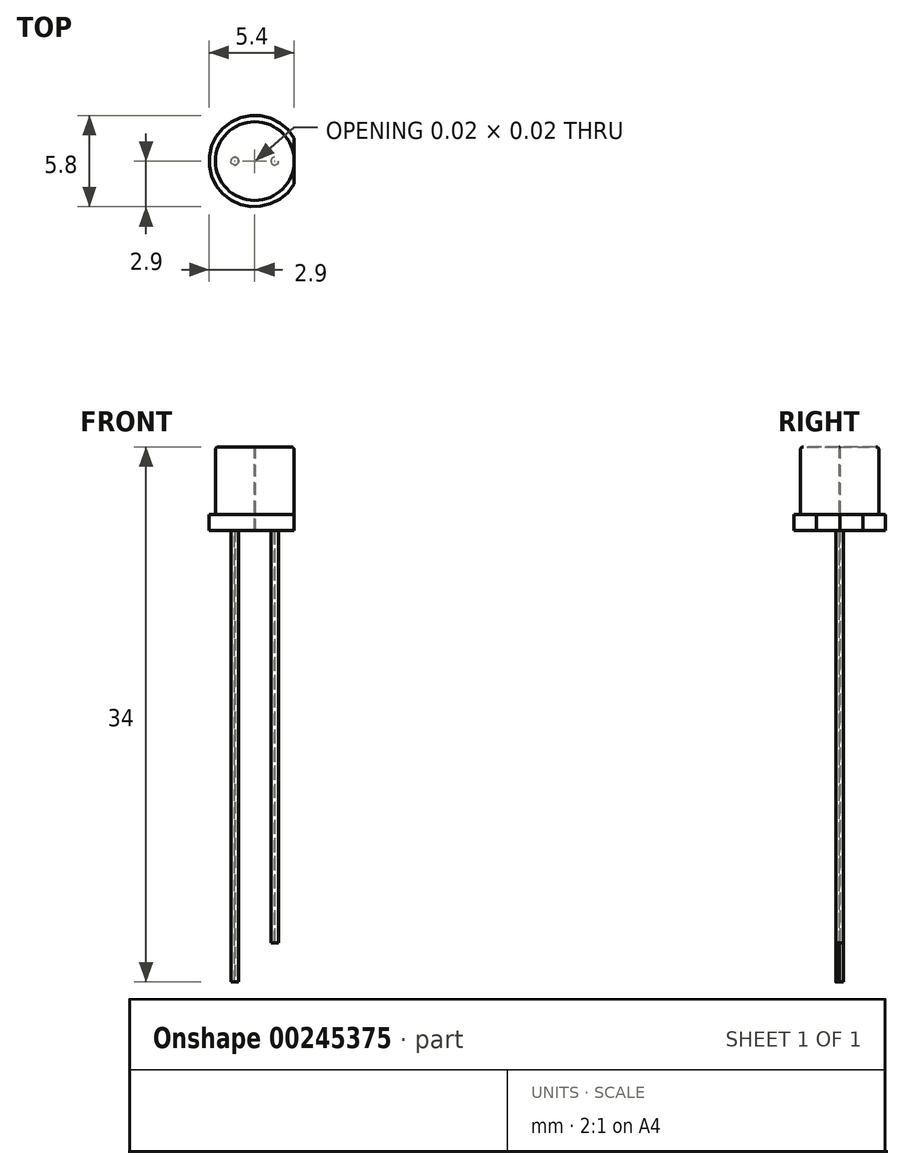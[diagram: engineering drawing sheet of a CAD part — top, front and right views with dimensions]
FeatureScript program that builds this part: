
annotation { "Feature Type Name" : "Feature", "Feature Type Description" : "" }
export const myFeature = defineFeature(function(context is Context, id is Id, definition is map)
    precondition{}
    {
        {
            var Q0;
            Q0=qCreatedBy(makeId("Front.planeOp"),FACE);
            var sketch = newSketch(context, id + "F0", { "sketchPlane" : qUnion([Q0])});
            skLineSegment(sketch, "E0", {"start": v(0, 0) * mm, "end": v(0, 4.3) * mm});
            skLineSegment(sketch, "E1", {"start": v(0, 4.3) * mm, "end": v(2.5, 4.3) * mm});
            skLineSegment(sketch, "E2", {"start": v(2.5, 4.3) * mm, "end": v(2.5, 0) * mm});
            skLineSegment(sketch, "E3", {"start": v(2.5, 0) * mm, "end": v(0, 0) * mm});
            skLineSegment(sketch, "E4", {"start": v(0, 0) * mm, "end": v(0, -1) * mm});
            skLineSegment(sketch, "E5", {"start": v(0, -1) * mm, "end": v(2.9, -1) * mm});
            skLineSegment(sketch, "E6", {"start": v(2.9, -1) * mm, "end": v(2.9, 0) * mm});
            skLineSegment(sketch, "E7", {"start": v(2.9, 0) * mm, "end": v(2.5, 0) * mm});
            skLineSegment(sketch, "E8", {"start": v(1.27, -1) * mm, "end": v(1.27, -27.2) * mm});
            skLineSegment(sketch, "E9", {"start": v(1.27, -27.2) * mm, "end": v(1.52, -27.2) * mm});
            skLineSegment(sketch, "E10", {"start": v(1.52, -27.2) * mm, "end": v(1.52, -1) * mm, "construction": true});
            skLineSegment(sketch, "E11", {"start": v(1.27, -27.2) * mm, "end": v(1.02, -27.2) * mm});
            skLineSegment(sketch, "E12", {"start": v(1.02, -27.2) * mm, "end": v(1.02, -1) * mm});
            skLineSegment(sketch, "E13.MirrorCS", {"start": v(-1.02, -27.2) * mm, "end": v(-1.02, -1) * mm});
            skLineSegment(sketch, "E14", {"start": v(-1.27, -1) * mm, "end": v(-1.02, -1) * mm});
            skLineSegment(sketch, "E15", {"start": v(-1.27, -29.7) * mm, "end": v(-1.02, -29.7) * mm});
            skLineSegment(sketch, "E16", {"start": v(-1.02, -29.7) * mm, "end": v(-1.02, -27.2) * mm});
            skLineSegment(sketch, "E17", {"start": v(-1.27, -29.7) * mm, "end": v(-1.27, -1) * mm});
            skSolve(sketch);
        }
        {
            var Q0;
            Q0=makeQuery(id+"F0.imprint","IMPRINT",FACE,{"disambiguationData":[TD([[makeQuery(id+"F0.imprint","IMPRINT",EDGE,{"derivedFrom":sQuery(id+"F0.wireOp",EDGE,"E0")}),-1.0]])]});
            var Q1;
            Q1=makeQuery(id+"F0.imprint","IMPRINT",FACE,{"disambiguationData":[TD([[makeQuery(id+"F0.imprint","IMPRINT",EDGE,{"derivedFrom":sQuery(id+"F0.wireOp",EDGE,"E3")}),1.0]])]});
            extrude(context, id + "F1", {"entities" : qUnion([Q0, Q1]), "depth" : 0.01 * mm});
        }
        {
            var Q0;
            Q0=makeQuery(id+"F1.opExtrude","CAP_FACE",FACE,{"disambiguationData":[OSD([sQuery(id+"F0.wireOp",EDGE,"E0"),sQuery(id+"F0.wireOp",EDGE,"E1"),sQuery(id+"F0.wireOp",EDGE,"E2"),sQuery(id+"F0.wireOp",EDGE,"E4"),sQuery(id+"F0.wireOp",EDGE,"E5"),sQuery(id+"F0.wireOp",EDGE,"E6"),sQuery(id+"F0.wireOp",EDGE,"E7")])],"isStart":false});
            var Q1;
            Q1=makeQuery(id+"F1.opExtrude","CAP_EDGE",EDGE,{"disambiguationData":[OSD([sQuery(id+"F0.wireOp",EDGE,"E0"),sQuery(id+"F0.wireOp",EDGE,"E4")])],"isStart":true});
            revolve(context, id + "F2", {"operationType" : NewBodyOperationType.ADD, "entities" : qUnion([Q0]), "axis" : qUnion([Q1]), "revolveType" : RevolveType.FULL});
        }
        {
            var Q0;
            Q0=qCreatedBy(makeId("Right.planeOp"),FACE);
            cPlane(context, id + "F3", {"entities" : qUnion([Q0]), "cplaneType" : CPlaneType.OFFSET, "offset" : 2.5 * mm, "width" : 150 * mm, "height" : 150 * mm});
        }
        {
            var Q0;
            Q0=qCreatedBy(id+"F3.planeOp",FACE);
            var sketch = newSketch(context, id + "F4", { "sketchPlane" : qUnion([Q0])});
            skLineSegment(sketch, "E18.bottom", {"start": v(1.5, -1.2) * mm, "end": v(-1.5, -1.2) * mm});
            skLineSegment(sketch, "E18.top", {"start": v(1.5, 1.2) * mm, "end": v(-1.5, 1.2) * mm});
            skLineSegment(sketch, "E18.left", {"start": v(1.5, -1.2) * mm, "end": v(1.5, 1.2) * mm});
            skLineSegment(sketch, "E18.right", {"start": v(-1.5, -1.2) * mm, "end": v(-1.5, 1.2) * mm});
            skPoint(sketch, "E18.middle", {"position": v(0, 0) * mm});
            skSolve(sketch);
        }
        {
            var Q0;
            Q0 = qSketchRegion(id + "F4", true);
            extrude(context, id + "F5", {"entities" : qUnion([Q0]), "operationType" : NewBodyOperationType.REMOVE, "depth" : 2 * mm});
        }
        {
            var Q0;
            {var subQ0=sQuery(id+"F0.wireOp",EDGE,"E8");Q0=makeQuery(id+"F0.imprint","IMPRINT",FACE,{"disambiguationData":[TD([[makeQuery(id+"F0.imprint","IMPRINT",EDGE,{"derivedFrom":subQ0}),-1.0]])]});}
            extrude(context, id + "F6", {"entities" : qUnion([Q0]), "operationType" : NewBodyOperationType.ADD, "depth" : 0.01 * mm});
        }
        {
            var Q0;
            Q0=makeQuery(id+"F0.imprint","IMPRINT",FACE,{"disambiguationData":[TD([[makeQuery(id+"F0.imprint","IMPRINT",EDGE,{"derivedFrom":sQuery(id+"F0.wireOp",EDGE,"E13.MirrorCS")}),1.0]])]});
            extrude(context, id + "F7", {"entities" : qUnion([Q0]), "operationType" : NewBodyOperationType.ADD, "depth" : 0.01 * mm});
        }
        {
            var Q0;
            Q0=makeQuery(id+"F7.opExtrude","CAP_FACE",FACE,{"disambiguationData":[OSD([sQuery(id+"F0.wireOp",EDGE,"E13.MirrorCS"),sQuery(id+"F0.wireOp",EDGE,"ac1886b3-cde3-48e8-9153-fe326fcb880c0.MirrorCS"),sQuery(id+"F0.wireOp",EDGE,"E14"),sQuery(id+"F0.wireOp",EDGE,"SvBCKN1I-MjCF-pU42-bqUf-L1uZbrdVZMYg"),sQuery(id+"F0.wireOp",EDGE,"E15"),sQuery(id+"F0.wireOp",EDGE,"E16")])],"isStart":false});
            var Q1;
            Q1=sQuery(id+"F0.wireOp",EDGE,"E17");
            revolve(context, id + "F8", {"operationType" : NewBodyOperationType.ADD, "entities" : qUnion([Q0]), "axis" : qUnion([Q1]), "revolveType" : RevolveType.FULL});
        }
        {
            var Q0;
            Q0=makeQuery(id+"F6.opExtrude","CAP_FACE",FACE,{"disambiguationData":[OSD([sQuery(id+"F0.wireOp",EDGE,"E5"),sQuery(id+"F0.wireOp",EDGE,"E8"),sQuery(id+"F0.wireOp",EDGE,"E11"),sQuery(id+"F0.wireOp",EDGE,"E12")])],"isStart":false});
            var Q1;
            Q1=sQuery(id+"F0.wireOp",EDGE,"E8");
            revolve(context, id + "F9", {"operationType" : NewBodyOperationType.ADD, "entities" : qUnion([Q0]), "axis" : qUnion([Q1]), "revolveType" : RevolveType.FULL});
        }
        {
            var Q0;
            Q0=makeQuery(id+"F2.opRevolve","SWEPT_EDGE",EDGE,{"disambiguationData":[OSD([sQuery(id+"F0.wireOp",EDGE,"E1"),sQuery(id+"F0.wireOp",EDGE,"E2")])]});
            fillet(context, id + "F10", {"entities" : qUnion([Q0]), "radius" : 0.2 * mm, "tangentPropagation" : true, "allowEdgeOverflow" : false});
        }
    });
